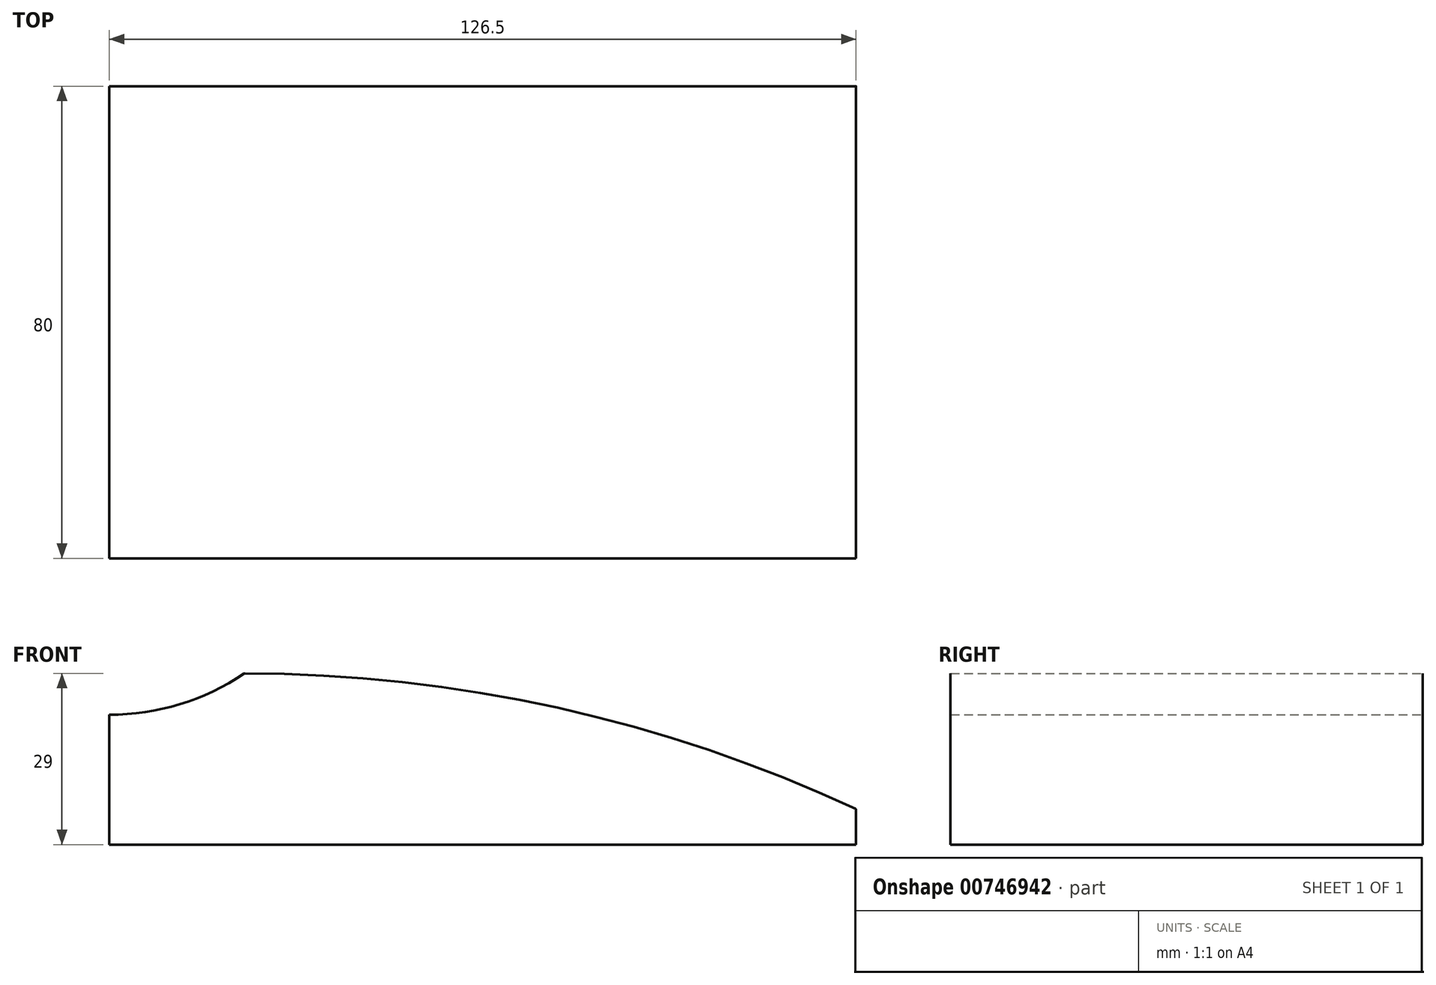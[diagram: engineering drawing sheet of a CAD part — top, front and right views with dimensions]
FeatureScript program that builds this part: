
annotation { "Feature Type Name" : "Feature", "Feature Type Description" : "" }
export const myFeature = defineFeature(function(context is Context, id is Id, definition is map)
    precondition{}
    {
        {
            var Q0;
            Q0=qCreatedBy(makeId("Front.planeOp"),FACE);
            var sketch = newSketch(context, id + "F0", { "sketchPlane" : qUnion([Q0])});
            skLineSegment(sketch, "E0", {"start": v(0, 0) * mm, "end": v(126.5, 0) * mm});
            skArc(sketch, "E1", {"start": v(0, 22) * mm, "mid": v(11.94, 23.78) * mm, "end": v(22.85, 28.97) * mm});
            skLineSegment(sketch, "E2", {"start": v(126.5, 0) * mm, "end": v(126.5, 5.87) * mm});
            skArc(sketch, "E3", {"start": v(126.38, 6.05) * mm, "mid": v(75.93, 23.19) * mm, "end": v(22.96, 29) * mm});
            skLineSegment(sketch, "E4", {"start": v(0, 20) * mm, "end": v(0, 22) * mm});
            skArc(sketch, "E5", {"start": v(126.5, 5.87) * mm, "mid": v(126.47, 5.98) * mm, "end": v(126.38, 6.05) * mm});
            skArc(sketch, "E6", {"start": v(22.96, 29) * mm, "mid": v(22.9, 29) * mm, "end": v(22.85, 28.97) * mm});
            skLineSegment(sketch, "E7", {"start": v(0, 20) * mm, "end": v(0, 0) * mm});
            skSolve(sketch);
        }
        {
            var Q0;
            Q0=makeQuery(id+"F0.imprint","IMPRINT",FACE,{"disambiguationData":[TD([[makeQuery(id+"F0.imprint","IMPRINT",EDGE,{"derivedFrom":sQuery(id+"F0.wireOp",EDGE,"E0")}),1.0]])]});
            extrude(context, id + "F1", {"entities" : qUnion([Q0]), "depth" : 80 * mm, "offsetDistance" : 25 * mm});
        }
    });
